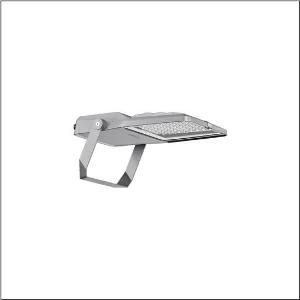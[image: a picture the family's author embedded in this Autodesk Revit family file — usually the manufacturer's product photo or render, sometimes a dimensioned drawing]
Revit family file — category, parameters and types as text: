
# Revit family: floodlight_fl_21_mini___pl64_5xa7776d4e1a_c051
name_source: partatom
category: Lighting Fixtures
units: mm (PartAtom-declared; Revit-internal decimal feet)

## family parameters
Cut with Voids When Loaded = No
Host = Face
Light Source = No
Part Type = Normal
Room Calculation Point = No
Round Connector Dimension = Use Diameter
Shared = No

## types (1)
- --- (1 x LED, 17960 lm, 142.9 W, 4000K)
    Apparent Load = 143 VA
    CIE Flux Codes = 28 80 98 100 100
    Color Rendering = 70
    Color Temperature = 4000K
    Default Elevation = 1800 mm
    Description = Floodlight FL 21 mini, floodlight, primary light control with lens, of PMMA, primary optical cover: protective disc, of toughened safety glass, transparent, light distribution: PL64, light emission: direct distribution, installation type: surface-mounted, LED, High Power LED, rated luminous flux: 17.960lm, luminous efficacy: 126lm/W, light colour: 740, colour temperature: 4000K, control gear: D4iSmart Interface (Zhaga), control: overheat protection, constant luminous flux control, time-dependent luminous flux control, flexible luminous flux parameterisation, pre-setting: logarithmic dimming characteristic, with terminal, 6-pole, mains connection: 220..240V, AC, 50/60Hz, start of lifetime: 143W, end of service life: 151W, reduction: 63W, mounting bracket, of diecast aluminium, powder-coated, SITECO metallic grey (DB 702S), corrosivity category C5 mid according to DIN EN ISO 12944, suitable for swimming pools, chlorine-resistant, sealing non-destructively replaceable, mounting bracket, of steel, galvanised, powder-coated, SITECO metallic grey (DB 702S), Smart Interface below and above, protection rating (complete): IP66, insulation class (complete): insulation class II (safety insulation), certification: CE, ENEC, VDE, protection symbol: D, impact resistance: IK08, permissible operating ambient temperature: -40..+40°C, permissible operating ambient temperature for outdoor applications: -40..+50°C, standard: DIN EN 12944, LABS conformity tested according to VDMA 24364:2018-05, packaging unit: 1 piece

Light Distribution: PL64
    Height = 70 mm
    Lamp = 1 x LED
    Lamp Light Flux = 17960 lm
    Lamp Power = 142.9 W
    Lamp count = 1
    Length = 485 mm
    Luminous efficacy = 126 lm/W
    Manufacturer = Siteco
    ModVariant = No
    Model = 5XA7776D4E1A
    Mounting Place = Pole
    Mounting Type = Pole annexe
    Number of Poles = 1
    OnlyDefault = Yes
    Power Factor = 1
    Product Name = Floodlight FL 21 mini | PL64
    Product group = floodlight | pylon annexe
    ProductGroupID = 6201
    Protection Class = Protection class II
    Protection Degree = IP 66
    RLX_Detail_Level = 1
    RLX_Emergency_Light_Flux = 0 lm
    RLX_Emergency_Type = 0
    RLX_Emergency_Type_DB = No
    RlxData = <blob elided: 96365 chars, md5=f701a00a>
    Socket = socket
    Standby Power = 0 W
    System Light Flux = 17960 lm
    System Power = 143 W
    Type Comments = factory setting: luminous flux: 100 % | dim-lin: 254 | 730 mA
    Type Image = l_1006845.jpg
    URL = http://relux.com
    VarID = @adj_101531
    Voltage = 0 V
    Weight = 0.00 kg
    Width = 337 mm

## geometry (parser evidence)
native form markers: Blend x4, Sweep x12
no freeform markers — native parametric forms only
